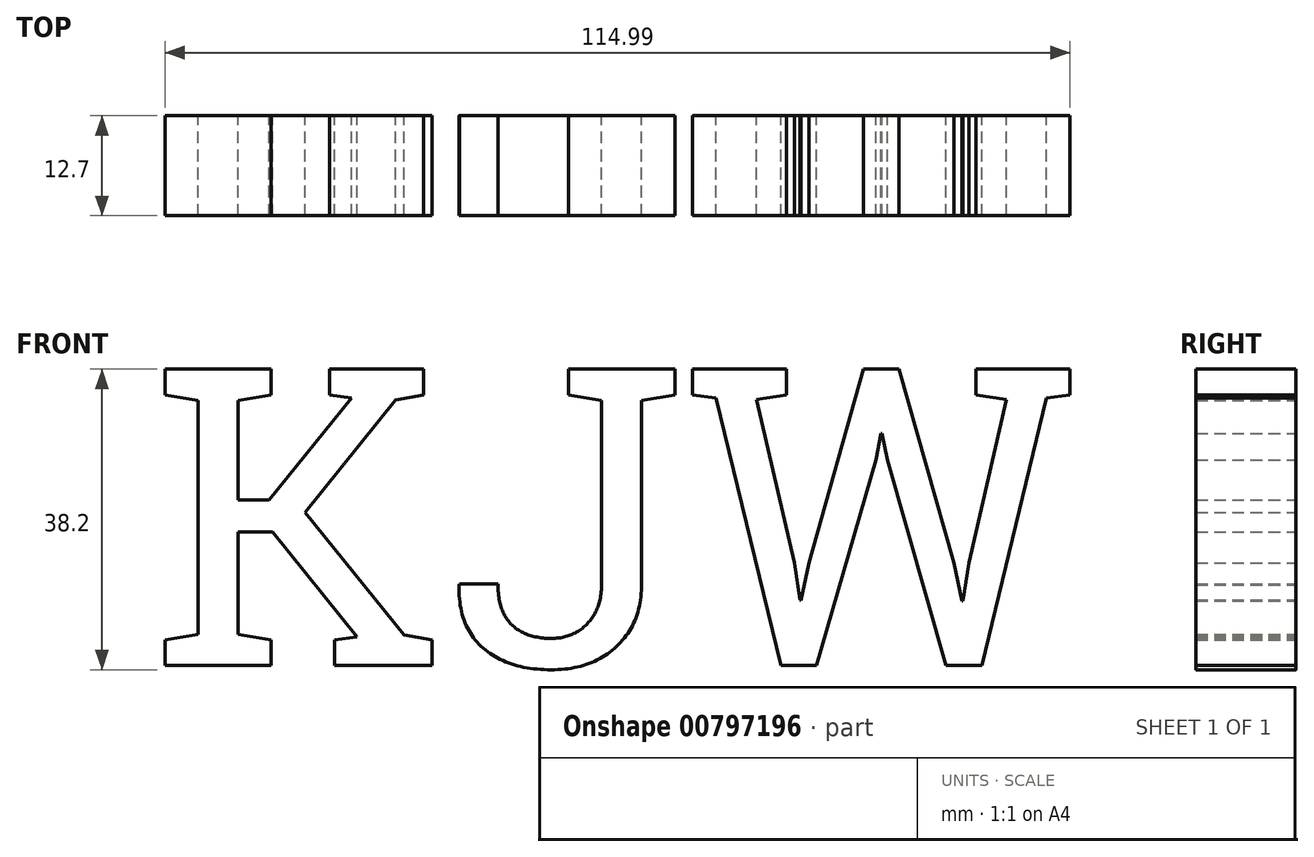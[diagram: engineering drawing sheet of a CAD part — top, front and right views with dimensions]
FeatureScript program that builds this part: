
annotation { "Feature Type Name" : "Feature", "Feature Type Description" : "" }
export const myFeature = defineFeature(function(context is Context, id is Id, definition is map)
    precondition{}
    {
        {
            var Q0;
            Q0=qCreatedBy(makeId("Front.planeOp"),FACE);
            var sketch = newSketch(context, id + "F0", { "sketchPlane" : qUnion([Q0])});
            skText(sketch, "E0", { "text": "KJW\n", "fontName": "RobotoSlab-Regular.ttf"});
            const initialGuessF0  = {"E0": [0.00245, -0.03813, 1, 0, 0.03813]};
            skSetInitialGuess(sketch, initialGuessF0);
            skSolve(sketch);
        }
        {
            var Q0;
            Q0 = qSketchRegion(id + "F0", true);
            extrude(context, id + "F1", {"entities" : qUnion([Q0]), "depth" : 12.7 * mm, "offsetDistance" : 25.4 * mm});
        }
    });
